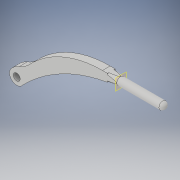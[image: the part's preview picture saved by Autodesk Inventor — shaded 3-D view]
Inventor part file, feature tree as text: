
AUTODESK INVENTOR PART (.ipt)
format: ipt  version: 2018.3 (Build 223284000, 284)  size: 161,792 bytes
history: native  units: in
note: dims shown in document units (in); Inventor stores cm internally (conversion verified against a paired STEP export)
features: sketch x2, extrude x2, revolve x1, plane x1
ambient origin geometry x8: Origin, YZ Plane, XZ Plane, XY Plane, X Axis, Y Axis, Z Axis, Center Point
bodies: Solid1 (feature_tree)
feature tree (6):
  sketch  "Sketch1"  dims[d0=0.096in d1=0.2in]
  extrude  "Extrusion1"  Depth=0.2in
  revolve  "Revolution1"  [1 undecoded]
  plane  "Work Plane1"
  extrude  "Extrusion2"  Depth=2.79in
  sketch  "Sketch2"  dims[d2=0.6in d3=0.15in d4=2.79in d5=1.186in d6=4.268in d7=1.618in d8=0.812in d9=0.113in d10=0.618in d11=2.015in d12=0.63in d13=0.107in d14=0.108in d17=0.107in d18=0.0in d19=0.13in d20=90.0deg d21=0.0in d22=0.13in d23=-0.0344in d24=0.13in d25=0.13in]
note: 1 required parameter value undecoded (feature->parameter linkage not recoverable at this tier; creation-order binding heuristic only, values carry confidence <= 0.55)
